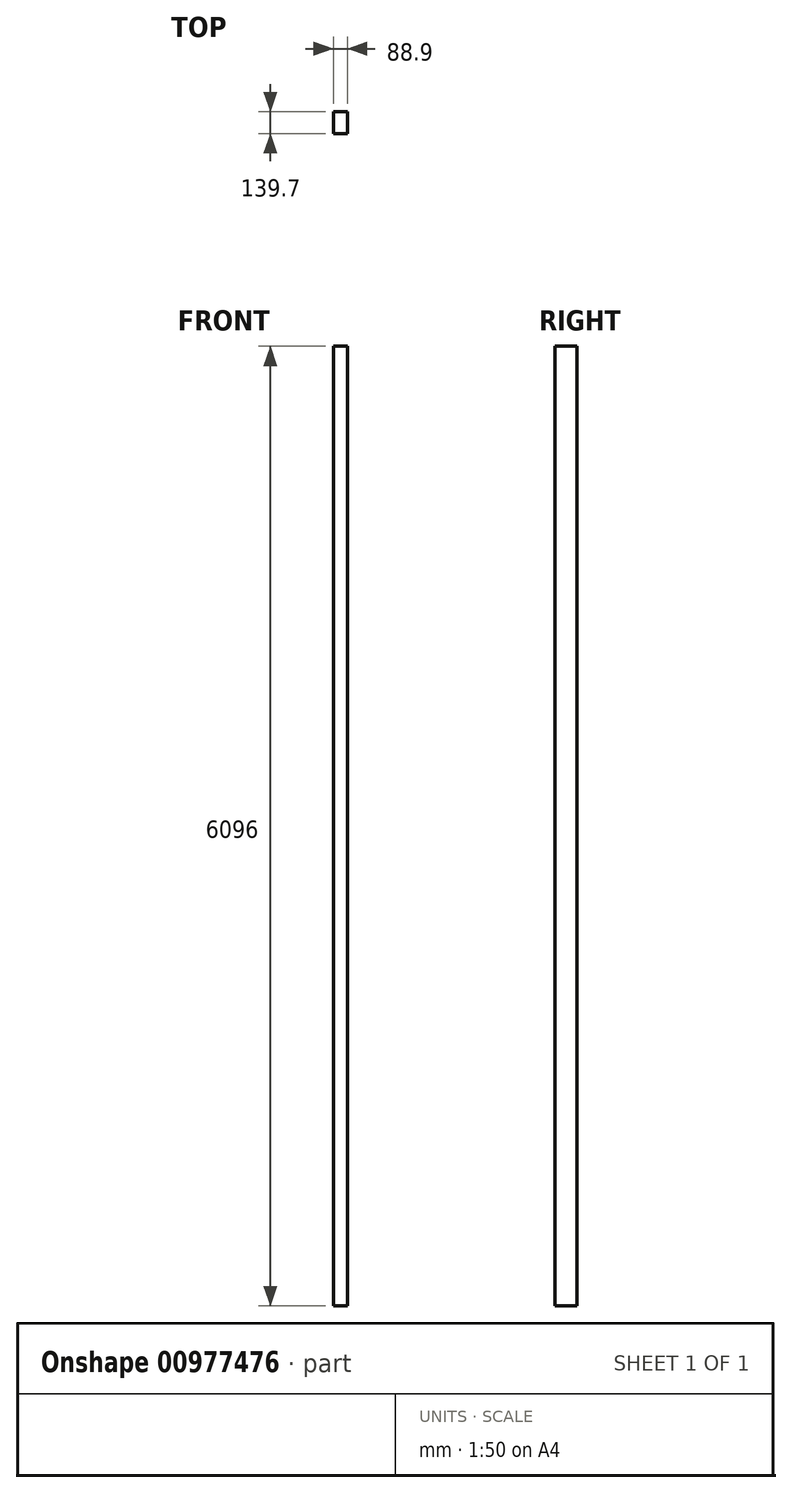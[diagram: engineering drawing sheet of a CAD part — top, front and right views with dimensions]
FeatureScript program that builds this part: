
annotation { "Feature Type Name" : "Feature", "Feature Type Description" : "" }
export const myFeature = defineFeature(function(context is Context, id is Id, definition is map)
    precondition{}
    {
        {
            var Q0;
            Q0=qCreatedBy(makeId("Top.planeOp"),FACE);
            var sketch = newSketch(context, id + "F0", { "sketchPlane" : qUnion([Q0])});
            skLineSegment(sketch, "E0.bottom", {"start": v(-88.9, 139.7) * mm, "end": v(0, 139.7) * mm});
            skLineSegment(sketch, "E0.top", {"start": v(-88.9, 0) * mm, "end": v(0, 0) * mm});
            skLineSegment(sketch, "E0.left", {"start": v(-88.9, 139.7) * mm, "end": v(-88.9, 0) * mm});
            skLineSegment(sketch, "E0.right", {"start": v(0, 139.7) * mm, "end": v(0, 0) * mm});
            skSolve(sketch);
        }
        {
            var Q0;
            Q0 = qSketchRegion(id + "F0", true);
            extrude(context, id + "F1", {"entities" : qUnion([Q0]), "depth" : 6096 * mm, "offsetDistance" : 25.4 * mm});
        }
    });
